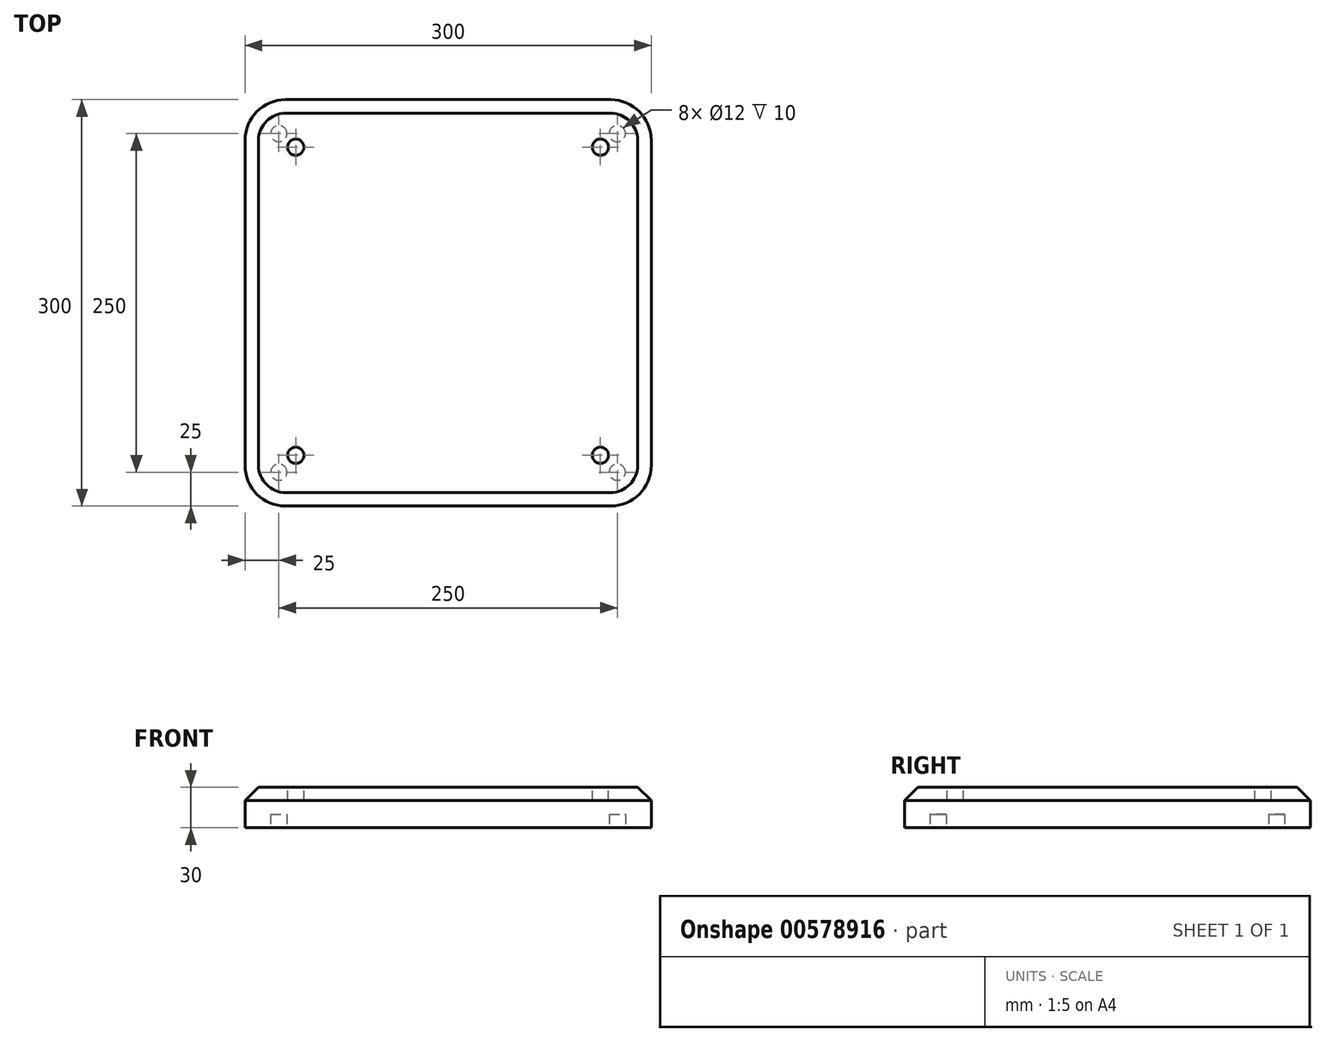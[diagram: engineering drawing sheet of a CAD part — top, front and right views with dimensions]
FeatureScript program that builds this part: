
annotation { "Feature Type Name" : "Feature", "Feature Type Description" : "" }
export const myFeature = defineFeature(function(context is Context, id is Id, definition is map)
    precondition{}
    {
        {
            var Q0;
            Q0=qCreatedBy(makeId("Top.planeOp"),FACE);
            var sketch = newSketch(context, id + "F0", { "sketchPlane" : qUnion([Q0])});
            skLineSegment(sketch, "E0.bottom", {"start": v(120, 150) * mm, "end": v(-120, 150) * mm});
            skLineSegment(sketch, "E0.top", {"start": v(120, -150) * mm, "end": v(-120, -150) * mm});
            skLineSegment(sketch, "E0.left", {"start": v(150, 120) * mm, "end": v(150, -120) * mm});
            skLineSegment(sketch, "E0.right", {"start": v(-150, 120) * mm, "end": v(-150, -120) * mm});
            skPoint(sketch, "E0.middle", {"position": v(0, 0) * mm});
            skPoint(sketch, "E1.visualSharp", {"position": v(-150, 150) * mm});
            skArc(sketch, "E1.filletArc", {"start": v(-120, 150) * mm, "mid": v(-141.21, 141.21) * mm, "end": v(-150, 120) * mm});
            skPoint(sketch, "E2.visualSharp", {"position": v(150, 150) * mm});
            skArc(sketch, "E2.filletArc", {"start": v(150, 120) * mm, "mid": v(141.21, 141.21) * mm, "end": v(120, 150) * mm});
            skPoint(sketch, "E3.visualSharp", {"position": v(150, -150) * mm});
            skArc(sketch, "E3.filletArc", {"start": v(120, -150) * mm, "mid": v(141.21, -141.21) * mm, "end": v(150, -120) * mm});
            skPoint(sketch, "E4.visualSharp", {"position": v(-150, -150) * mm});
            skArc(sketch, "E4.filletArc", {"start": v(-150, -120) * mm, "mid": v(-141.21, -141.21) * mm, "end": v(-120, -150) * mm});
            skSolve(sketch);
        }
        {
            var Q0;
            Q0=makeQuery(id+"F0.imprint","IMPRINT",FACE,{"disambiguationData":[TD([[makeQuery(id+"F0.imprint","IMPRINT",EDGE,{"derivedFrom":sQuery(id+"F0.wireOp",EDGE,"E0.bottom")}),1.0]])]});
            extrude(context, id + "F1", {"entities" : qUnion([Q0]), "depth" : 30 * mm, "offsetDistance" : 25 * mm});
        }
        {
            var Q0;
            Q0=makeQuery(id+"F1.opExtrude","CAP_FACE",FACE,{"disambiguationData":[OSD([sQuery(id+"F0.wireOp",EDGE,"E0.bottom"),sQuery(id+"F0.wireOp",EDGE,"E0.top"),sQuery(id+"F0.wireOp",EDGE,"E0.left"),sQuery(id+"F0.wireOp",EDGE,"E0.right"),sQuery(id+"F0.wireOp",EDGE,"E1.filletArc"),sQuery(id+"F0.wireOp",EDGE,"E2.filletArc"),sQuery(id+"F0.wireOp",EDGE,"E3.filletArc"),sQuery(id+"F0.wireOp",EDGE,"E4.filletArc")])],"isStart":false});
            chamfer(context, id + "F2", {"entities" : qUnion([Q0]), "width" : 10 * mm, "tangentPropagation" : true});
        }
        {
            var Q0;
            Q0=makeQuery(id+"F1.opExtrude","CAP_FACE",FACE,{"disambiguationData":[OSD([sQuery(id+"F0.wireOp",EDGE,"E0.bottom"),sQuery(id+"F0.wireOp",EDGE,"E0.top"),sQuery(id+"F0.wireOp",EDGE,"E0.left"),sQuery(id+"F0.wireOp",EDGE,"E0.right"),sQuery(id+"F0.wireOp",EDGE,"E1.filletArc"),sQuery(id+"F0.wireOp",EDGE,"E2.filletArc"),sQuery(id+"F0.wireOp",EDGE,"E3.filletArc"),sQuery(id+"F0.wireOp",EDGE,"E4.filletArc")])],"isStart":false});
            var sketch = newSketch(context, id + "F3", { "sketchPlane" : qUnion([Q0])});
            skCircle(sketch, "E5", {"center": v(-112.5, 114.92) * mm, "radius": 6 * mm});
            skCircle(sketch, "E6", {"center": v(112.5, 114.92) * mm, "radius": 6 * mm});
            skCircle(sketch, "E7", {"center": v(112.5, -112.5) * mm, "radius": 6 * mm});
            skCircle(sketch, "E8", {"center": v(-112.5, -112.5) * mm, "radius": 6 * mm});
            skSolve(sketch);
        }
        {
            var Q0;
            Q0=makeQuery(id+"F3.imprint","IMPRINT",FACE,{"disambiguationData":[TD([[makeQuery(id+"F3.imprint","IMPRINT",EDGE,{"derivedFrom":sQuery(id+"F3.wireOp",EDGE,"E6")}),1.0]])]});
            var Q1;
            Q1=makeQuery(id+"F3.imprint","IMPRINT",FACE,{"disambiguationData":[TD([[makeQuery(id+"F3.imprint","IMPRINT",EDGE,{"derivedFrom":sQuery(id+"F3.wireOp",EDGE,"E5")}),1.0]])]});
            var Q2;
            Q2=makeQuery(id+"F3.imprint","IMPRINT",FACE,{"disambiguationData":[TD([[makeQuery(id+"F3.imprint","IMPRINT",EDGE,{"derivedFrom":sQuery(id+"F3.wireOp",EDGE,"E8")}),1.0]])]});
            var Q3;
            Q3=makeQuery(id+"F3.imprint","IMPRINT",FACE,{"disambiguationData":[TD([[makeQuery(id+"F3.imprint","IMPRINT",EDGE,{"derivedFrom":sQuery(id+"F3.wireOp",EDGE,"E7")}),1.0]])]});
            extrude(context, id + "F4", {"entities" : qUnion([Q0, Q1, Q2, Q3]), "operationType" : NewBodyOperationType.REMOVE, "oppositeDirection" : true, "depth" : 10 * mm, "offsetDistance" : 25 * mm});
        }
        {
            var Q0;
            Q0=makeQuery(id+"F1.opExtrude","CAP_FACE",FACE,{"disambiguationData":[OSD([sQuery(id+"F0.wireOp",EDGE,"E0.bottom"),sQuery(id+"F0.wireOp",EDGE,"E0.top"),sQuery(id+"F0.wireOp",EDGE,"E0.left"),sQuery(id+"F0.wireOp",EDGE,"E0.right"),sQuery(id+"F0.wireOp",EDGE,"E1.filletArc"),sQuery(id+"F0.wireOp",EDGE,"E2.filletArc"),sQuery(id+"F0.wireOp",EDGE,"E3.filletArc"),sQuery(id+"F0.wireOp",EDGE,"E4.filletArc")])],"isStart":true});
            var sketch = newSketch(context, id + "F5", { "sketchPlane" : qUnion([Q0])});
            skCircle(sketch, "E9", {"center": v(125, -125) * mm, "radius": 6 * mm});
            skCircle(sketch, "E10", {"center": v(125, 125) * mm, "radius": 6 * mm});
            skCircle(sketch, "E11", {"center": v(-125, 125) * mm, "radius": 6 * mm});
            skCircle(sketch, "E12", {"center": v(-125, -125) * mm, "radius": 6 * mm});
            skSolve(sketch);
        }
        {
            var Q0;
            Q0=makeQuery(id+"F5.imprint","IMPRINT",FACE,{"disambiguationData":[TD([[makeQuery(id+"F5.imprint","IMPRINT",EDGE,{"derivedFrom":sQuery(id+"F5.wireOp",EDGE,"E12")}),1.0]])]});
            var Q1;
            Q1=makeQuery(id+"F5.imprint","IMPRINT",FACE,{"disambiguationData":[TD([[makeQuery(id+"F5.imprint","IMPRINT",EDGE,{"derivedFrom":sQuery(id+"F5.wireOp",EDGE,"E11")}),1.0]])]});
            var Q2;
            Q2=makeQuery(id+"F5.imprint","IMPRINT",FACE,{"disambiguationData":[TD([[makeQuery(id+"F5.imprint","IMPRINT",EDGE,{"derivedFrom":sQuery(id+"F5.wireOp",EDGE,"E9")}),1.0]])]});
            var Q3;
            Q3=makeQuery(id+"F5.imprint","IMPRINT",FACE,{"disambiguationData":[TD([[makeQuery(id+"F5.imprint","IMPRINT",EDGE,{"derivedFrom":sQuery(id+"F5.wireOp",EDGE,"E10")}),1.0]])]});
            extrude(context, id + "F6", {"entities" : qUnion([Q0, Q1, Q2, Q3]), "operationType" : NewBodyOperationType.REMOVE, "oppositeDirection" : true, "depth" : 10 * mm, "offsetDistance" : 25 * mm});
        }
    });
